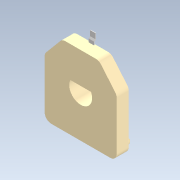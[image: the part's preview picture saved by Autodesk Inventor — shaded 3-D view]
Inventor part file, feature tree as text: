
AUTODESK INVENTOR PART (.ipt)
format: ipt  version: 2020.2 (Build 242310000, 310)  size: 187,392 bytes
history: native  units: mm
features: extrude x4, sketch x4, pattern_linear x2, fillet x1, mirror x1
ambient origin geometry x8: Origin, YZ Plane, XZ Plane, XY Plane, X Axis, Y Axis, Z Axis, Center Point
bodies: Solid1 (feature_tree)
feature tree (12):
  extrude  "Extrusion1"  Depth=11.0mm
  extrude  "Extrusion2"  Depth=1.0mm
  fillet  "Fillet1"  Radius=1.0mm
  extrude  "Extrusion3"  Depth=12.0mm
  extrude  "Extrusion4"  Depth=2.0mm
  mirror  "Mirror1"
  pattern_linear  "Rectangular Pattern1"  Spacing1=6.981317mm  [1 undecoded]
  pattern_linear  "Rectangular Pattern2"  Spacing1=1.85mm  [1 undecoded]
  sketch  "Sketch1"  dims[d0=11.0mm d2=6.5mm]
  sketch  "Sketch2"  dims[d3=3.5mm d4=1.0mm d9=1.0mm]
  sketch  "Sketch3"  dims[d10=12.0mm d11=3.58mm]
  sketch  "Sketch4"  dims[d12=3.58mm d13=6.981317mm d14=6.981317mm d15=1.85mm d16=0.0mm d17=1.0mm d18=1.0mm d19=1.0mm d20=0.0mm d21=0.5mm d22=0.5mm d23=1.0mm d24=0.0mm d25=0.1mm d29=0.1mm d30=0.8mm d31=0.0mm d32=20.0mm d34=2.0mm d35=20.0mm d37=2.0mm]
note: 2 required parameter values undecoded (feature->parameter linkage not recoverable at this tier; creation-order binding heuristic only, values carry confidence <= 0.55)
